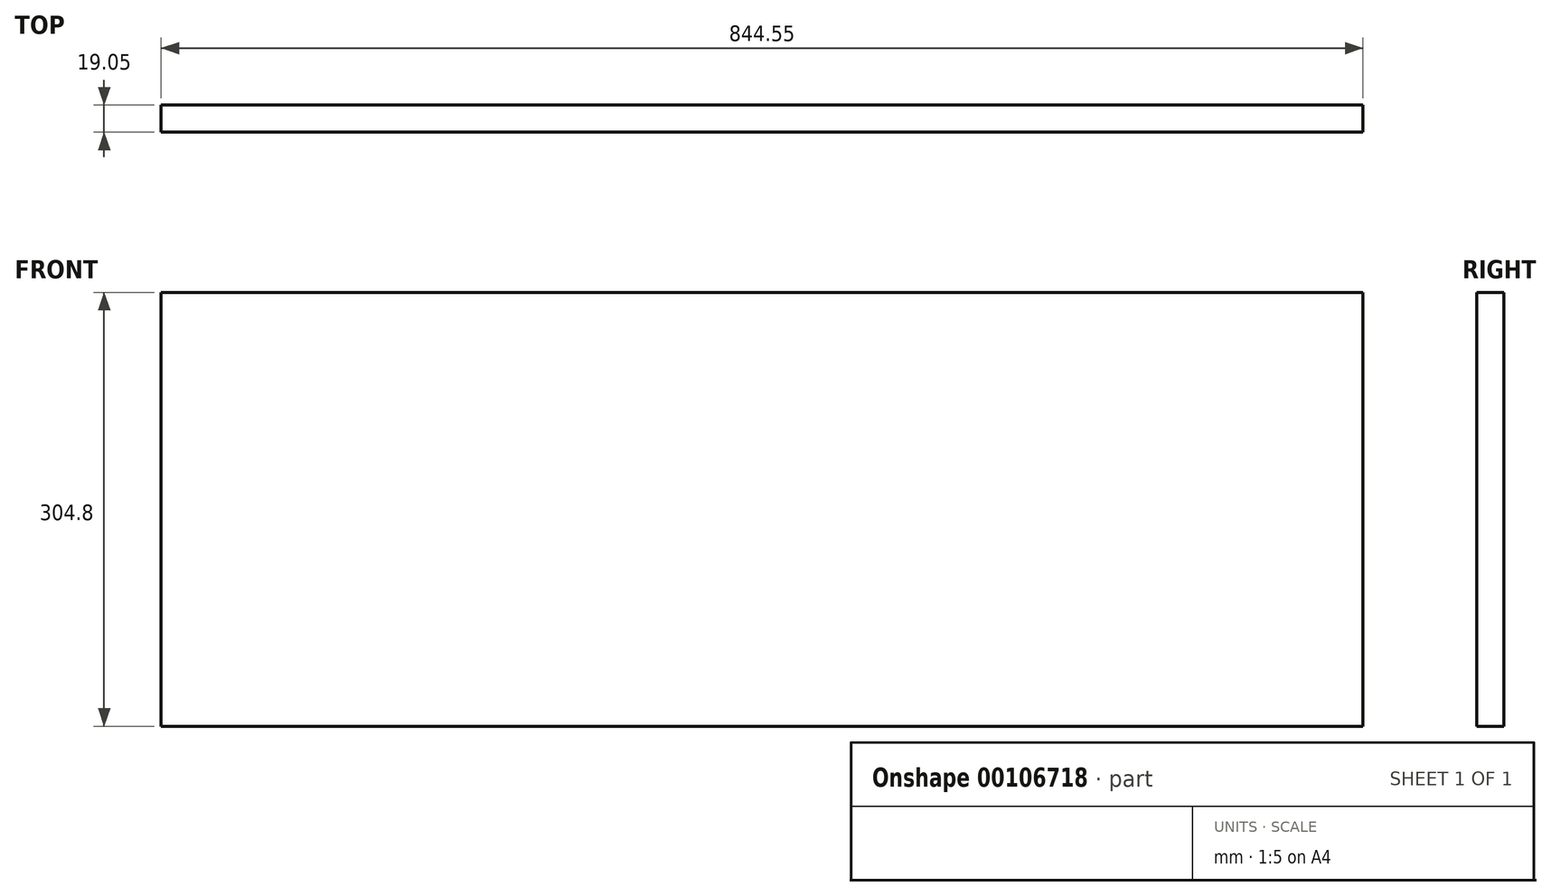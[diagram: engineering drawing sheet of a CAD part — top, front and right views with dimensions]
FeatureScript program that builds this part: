
annotation { "Feature Type Name" : "Feature", "Feature Type Description" : "" }
export const myFeature = defineFeature(function(context is Context, id is Id, definition is map)
    precondition{}
    {
        {
            var Q0;
            Q0=qCreatedBy(makeId("Front.planeOp"),FACE);
            var sketch = newSketch(context, id + "F0", { "sketchPlane" : qUnion([Q0])});
            skLineSegment(sketch, "E0.bottom", {"start": v(0, 0) * mm, "end": v(844.55, 0) * mm});
            skLineSegment(sketch, "E0.top", {"start": v(0, 304.8) * mm, "end": v(844.55, 304.8) * mm});
            skLineSegment(sketch, "E0.left", {"start": v(0, 0) * mm, "end": v(0, 304.8) * mm});
            skLineSegment(sketch, "E0.right", {"start": v(844.55, 0) * mm, "end": v(844.55, 304.8) * mm});
            skSolve(sketch);
        }
        {
            var Q0;
            Q0=makeQuery(id+"F0.imprint","IMPRINT",FACE,{"disambiguationData":[TD([[makeQuery(id+"F0.imprint","IMPRINT",EDGE,{"derivedFrom":sQuery(id+"F0.wireOp",EDGE,"E0.bottom")}),1.0]])]});
            extrude(context, id + "F1", {"entities" : qUnion([Q0]), "depth" : 19.05 * mm});
        }
    });
